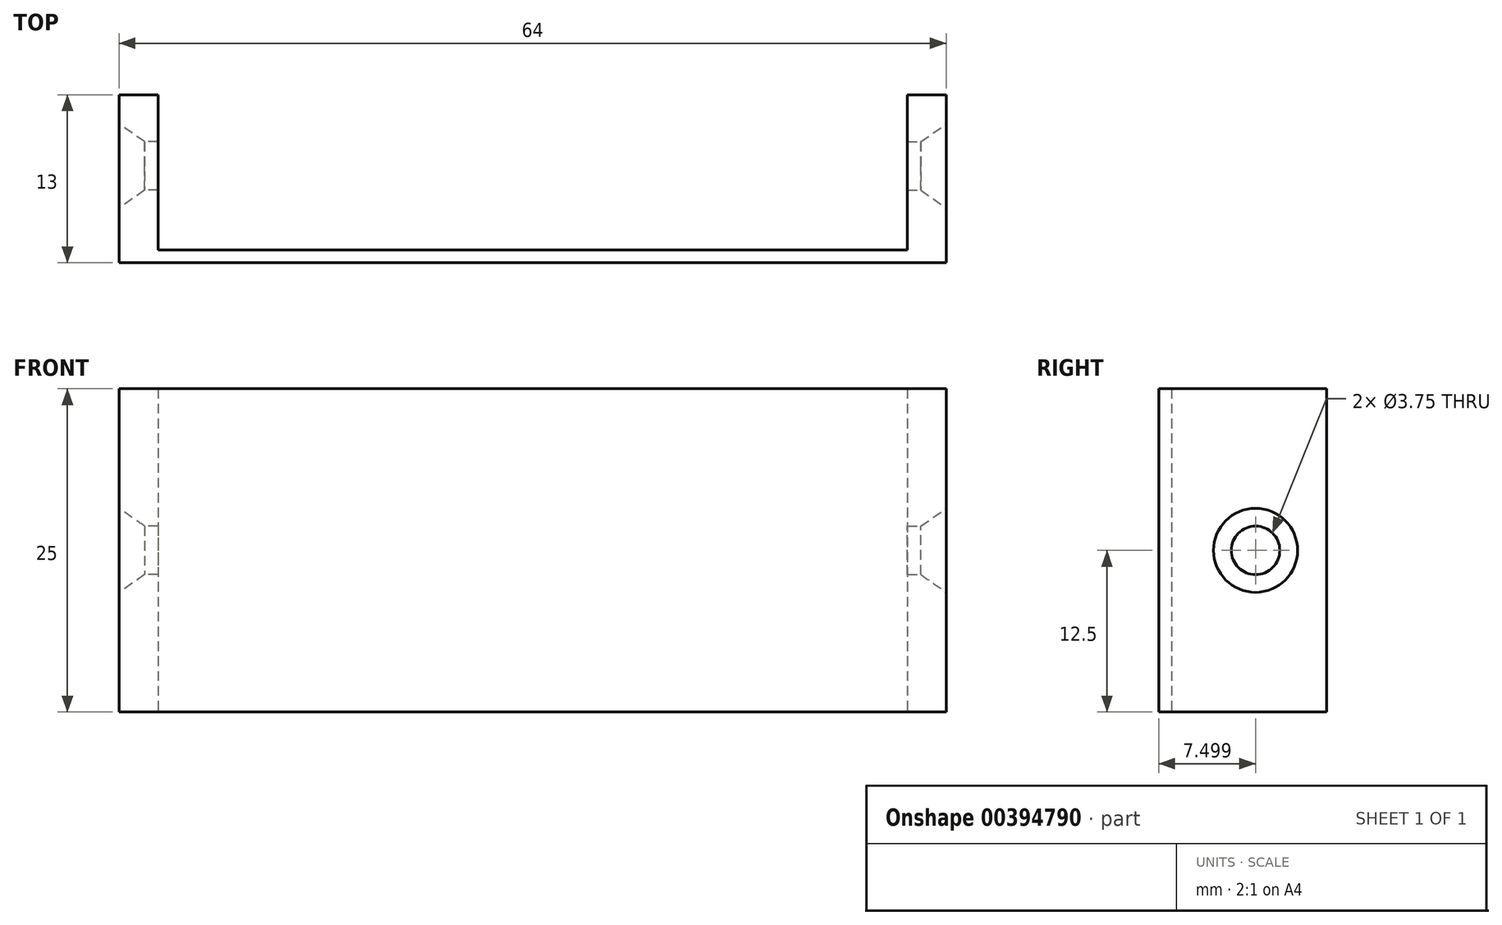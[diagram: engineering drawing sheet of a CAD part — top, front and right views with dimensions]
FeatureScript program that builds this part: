
annotation { "Feature Type Name" : "Feature", "Feature Type Description" : "" }
export const myFeature = defineFeature(function(context is Context, id is Id, definition is map)
    precondition{}
    {
        {
            var Q0;
            Q0=qCreatedBy(makeId("Top.planeOp"),FACE);
            var sketch = newSketch(context, id + "F0", { "sketchPlane" : qUnion([Q0])});
            skLineSegment(sketch, "E0", {"start": v(-26.2, 6.95) * mm, "end": v(-26.2, -6.05) * mm});
            skLineSegment(sketch, "E1", {"start": v(-26.2, -6.05) * mm, "end": v(37.8, -6.05) * mm});
            skLineSegment(sketch, "E2", {"start": v(37.8, -6.05) * mm, "end": v(37.8, 6.95) * mm});
            skLineSegment(sketch, "E3", {"start": v(37.8, 6.95) * mm, "end": v(34.8, 6.95) * mm});
            skLineSegment(sketch, "E4", {"start": v(34.8, 6.95) * mm, "end": v(34.8, -5.05) * mm});
            skLineSegment(sketch, "E5", {"start": v(34.8, -5.05) * mm, "end": v(-23.2, -5.05) * mm});
            skLineSegment(sketch, "E6", {"start": v(-23.2, -5.05) * mm, "end": v(-23.2, 6.95) * mm});
            skLineSegment(sketch, "E7", {"start": v(-23.2, 6.95) * mm, "end": v(-26.2, 6.95) * mm});
            skSolve(sketch);
        }
        {
            var Q0;
            Q0=makeQuery(id+"F0.imprint","IMPRINT",FACE,{"disambiguationData":[TD([[makeQuery(id+"F0.imprint","IMPRINT",EDGE,{"derivedFrom":sQuery(id+"F0.wireOp",EDGE,"E0")}),1.0]])]});
            extrude(context, id + "F1", {"entities" : qUnion([Q0]), "depth" : 25 * mm});
        }
        {
            var Q0;
            Q0=makeQuery(id+"F1.opExtrude","SWEPT_FACE",FACE,{"disambiguationData":[OSD([sQuery(id+"F0.wireOp",EDGE,"E0")])]});
            var sketch = newSketch(context, id + "F2", { "sketchPlane" : qUnion([Q0])});
            skPoint(sketch, "E8", {"position": v(-1.45, 12.5) * mm});
            skSolve(sketch);
        }
        {
            var Q0;
            Q0=sQuery(id+"F2.wireOp",VERTEX,"E8");
            var Q1;
            Q1=makeQuery(id+"F1.opExtrude","SWEPT_BODY",BODY,{"disambiguationData":[OSD([sQuery(id+"F0.wireOp",EDGE,"E0"),sQuery(id+"F0.wireOp",EDGE,"E1"),sQuery(id+"F0.wireOp",EDGE,"E2"),sQuery(id+"F0.wireOp",EDGE,"E3"),sQuery(id+"F0.wireOp",EDGE,"E4"),sQuery(id+"F0.wireOp",EDGE,"E5"),sQuery(id+"F0.wireOp",EDGE,"E6"),sQuery(id+"F0.wireOp",EDGE,"E7")])]});
            hole(context, id + "F3", {"style" : HoleStyle.C_SINK, "endStyle" : HoleEndStyle.BLIND, "holeDiameter" : 3.75 * mm, "cSinkDiameter" : 6.5 * mm, "cSinkAngle" : 70 * degree, "holeDepth" : 6 * mm, "tappedDepth" : 12 * mm, "tapClearance" : 3, "startFromSketch" : true, "locations" : qUnion([Q0]), "scope" : qUnion([Q1])});
        }
        {
            var Q0;
            Q0=makeQuery(id+"F1.opExtrude","SWEPT_FACE",FACE,{"disambiguationData":[OSD([sQuery(id+"F0.wireOp",EDGE,"E2")])]});
            var sketch = newSketch(context, id + "F4", { "sketchPlane" : qUnion([Q0])});
            skPoint(sketch, "E9", {"position": v(1.45, 12.5) * mm});
            skSolve(sketch);
        }
        {
            var Q0;
            Q0=sQuery(id+"F4.wireOp",VERTEX,"E9");
            var Q1;
            Q1=makeQuery(id+"F1.opExtrude","SWEPT_BODY",BODY,{"disambiguationData":[OSD([sQuery(id+"F0.wireOp",EDGE,"E0"),sQuery(id+"F0.wireOp",EDGE,"E1"),sQuery(id+"F0.wireOp",EDGE,"E2"),sQuery(id+"F0.wireOp",EDGE,"E3"),sQuery(id+"F0.wireOp",EDGE,"E4"),sQuery(id+"F0.wireOp",EDGE,"E5"),sQuery(id+"F0.wireOp",EDGE,"E6"),sQuery(id+"F0.wireOp",EDGE,"E7")])]});
            hole(context, id + "F5", {"style" : HoleStyle.C_SINK, "endStyle" : HoleEndStyle.BLIND, "holeDiameter" : 3.75 * mm, "cSinkDiameter" : 6.5 * mm, "cSinkAngle" : 70 * degree, "holeDepth" : 6 * mm, "tappedDepth" : 12 * mm, "tapClearance" : 3, "startFromSketch" : true, "locations" : qUnion([Q0]), "scope" : qUnion([Q1])});
        }
    });
